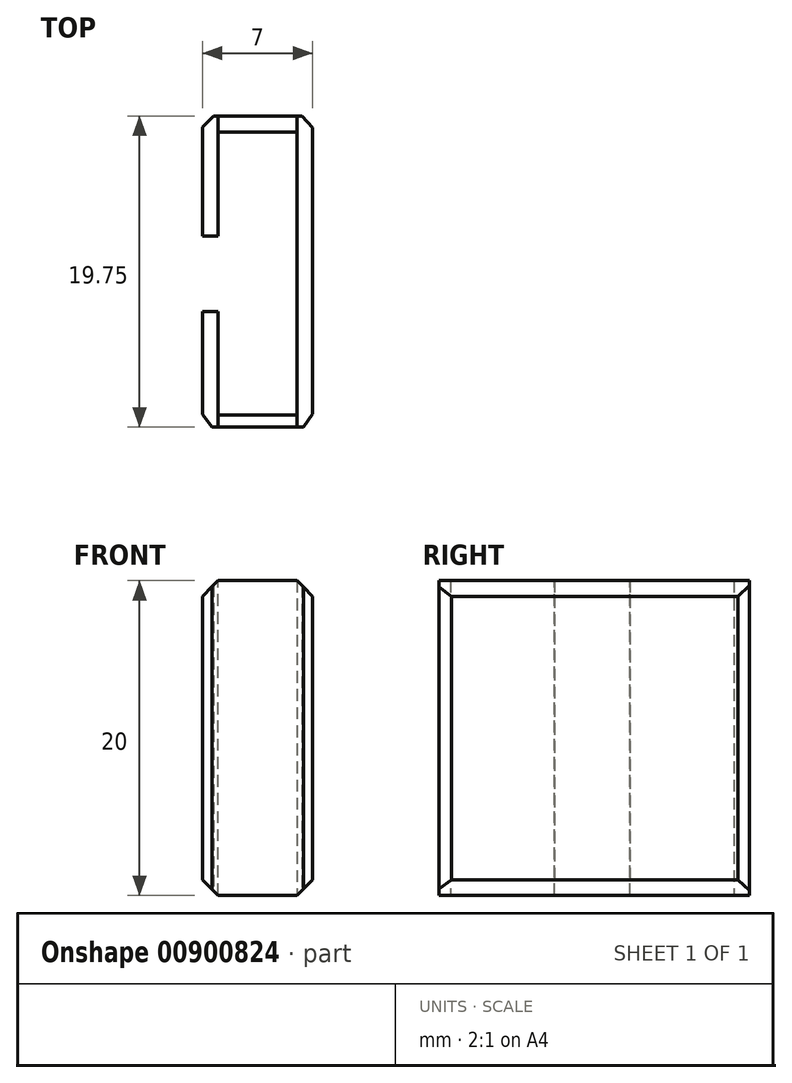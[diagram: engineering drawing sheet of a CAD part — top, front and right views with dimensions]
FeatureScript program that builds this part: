
annotation { "Feature Type Name" : "Feature", "Feature Type Description" : "" }
export const myFeature = defineFeature(function(context is Context, id is Id, definition is map)
    precondition{}
    {
        {
            var Q0;
            Q0=qCreatedBy(makeId("Top.planeOp"),FACE);
            var sketch = newSketch(context, id + "F0", { "sketchPlane" : qUnion([Q0])});
            skLineSegment(sketch, "E0.bottom", {"start": v(-7.93, 7.6) * mm, "end": v(-2.32, 7.6) * mm});
            skLineSegment(sketch, "E0.top", {"start": v(-8.02, -12.14) * mm, "end": v(-2.23, -12.14) * mm});
            skLineSegment(sketch, "E0.left", {"start": v(-8.64, 6.9) * mm, "end": v(-8.64, -11.35) * mm});
            skLineSegment(sketch, "E0.right", {"start": v(-1.64, 6.87) * mm, "end": v(-1.64, -11.33) * mm});
            skLineSegment(sketch, "E1.bottom", {"start": v(-7.64, 6.6) * mm, "end": v(-2.64, 6.6) * mm});
            skLineSegment(sketch, "E1.top", {"start": v(-7.64, -11.4) * mm, "end": v(-2.64, -11.4) * mm});
            skLineSegment(sketch, "E1.left", {"start": v(-7.64, 6.6) * mm, "end": v(-7.64, -11.4) * mm});
            skLineSegment(sketch, "E1.right", {"start": v(-2.64, 6.6) * mm, "end": v(-2.64, -11.4) * mm});
            skLineSegment(sketch, "E2", {"start": v(-8.64, 6.9) * mm, "end": v(-7.93, 7.6) * mm});
            skLineSegment(sketch, "E3", {"start": v(-2.32, 7.6) * mm, "end": v(-1.64, 6.87) * mm});
            skLineSegment(sketch, "E4", {"start": v(-8.02, -12.14) * mm, "end": v(-8.64, -11.35) * mm});
            skLineSegment(sketch, "E5", {"start": v(-2.23, -12.14) * mm, "end": v(-1.64, -11.33) * mm});
            skPoint(sketch, "E6.orphan", {"position": v(-1.64, -12.14) * mm});
            skPoint(sketch, "E7.orphan", {"position": v(-8.64, -12.14) * mm});
            skSolve(sketch);
        }
        {
            var Q0;
            Q0 = qSketchRegion(id + "F0", true);
            extrude(context, id + "F1", {"entities" : qUnion([Q0]), "depth" : 20 * mm, "offsetDistance" : 25 * mm});
        }
        {
            var Q0;
            Q0=makeQuery(id+"F1.opExtrude","CAP_EDGE",EDGE,{"disambiguationData":[OSD([sQuery(id+"F0.wireOp",EDGE,"E0.left")])],"isStart":false});
            var Q1;
            Q1=makeQuery(id+"F1.opExtrude","CAP_EDGE",EDGE,{"disambiguationData":[OSD([sQuery(id+"F0.wireOp",EDGE,"E0.left")])],"isStart":true});
            var Q2;
            Q2=makeQuery(id+"F1.opExtrude","CAP_EDGE",EDGE,{"disambiguationData":[OSD([sQuery(id+"F0.wireOp",EDGE,"E0.right")])],"isStart":true});
            var Q3;
            Q3=makeQuery(id+"F1.opExtrude","CAP_EDGE",EDGE,{"disambiguationData":[OSD([sQuery(id+"F0.wireOp",EDGE,"E0.right")])],"isStart":false});
            chamfer(context, id + "F2", {"entities" : qUnion([Q0, Q1, Q2, Q3]), "width" : 1 * mm, "tangentPropagation" : true});
        }
        {
            var Q0;
            Q0=makeQuery(id+"F1.opExtrude","SWEPT_FACE",FACE,{"disambiguationData":[OSD([sQuery(id+"F0.wireOp",EDGE,"E0.left")])]});
            var sketch = newSketch(context, id + "F3", { "sketchPlane" : qUnion([Q0])});
            skLineSegment(sketch, "E8.bottom", {"start": v(4.8, 20.66) * mm, "end": v(0, 20.66) * mm});
            skLineSegment(sketch, "E8.top", {"start": v(4.8, -0.93) * mm, "end": v(0, -0.93) * mm});
            skLineSegment(sketch, "E8.left", {"start": v(4.8, 20.66) * mm, "end": v(4.8, -0.93) * mm});
            skLineSegment(sketch, "E8.right", {"start": v(0, 20.66) * mm, "end": v(0, -0.93) * mm});
            skSolve(sketch);
        }
        {
            var Q0;
            Q0 = qSketchRegion(id + "F3", true);
            extrude(context, id + "F4", {"entities" : qUnion([Q0]), "operationType" : NewBodyOperationType.REMOVE, "oppositeDirection" : true, "depth" : 5 * mm, "offsetDistance" : 25 * mm});
        }
    });
